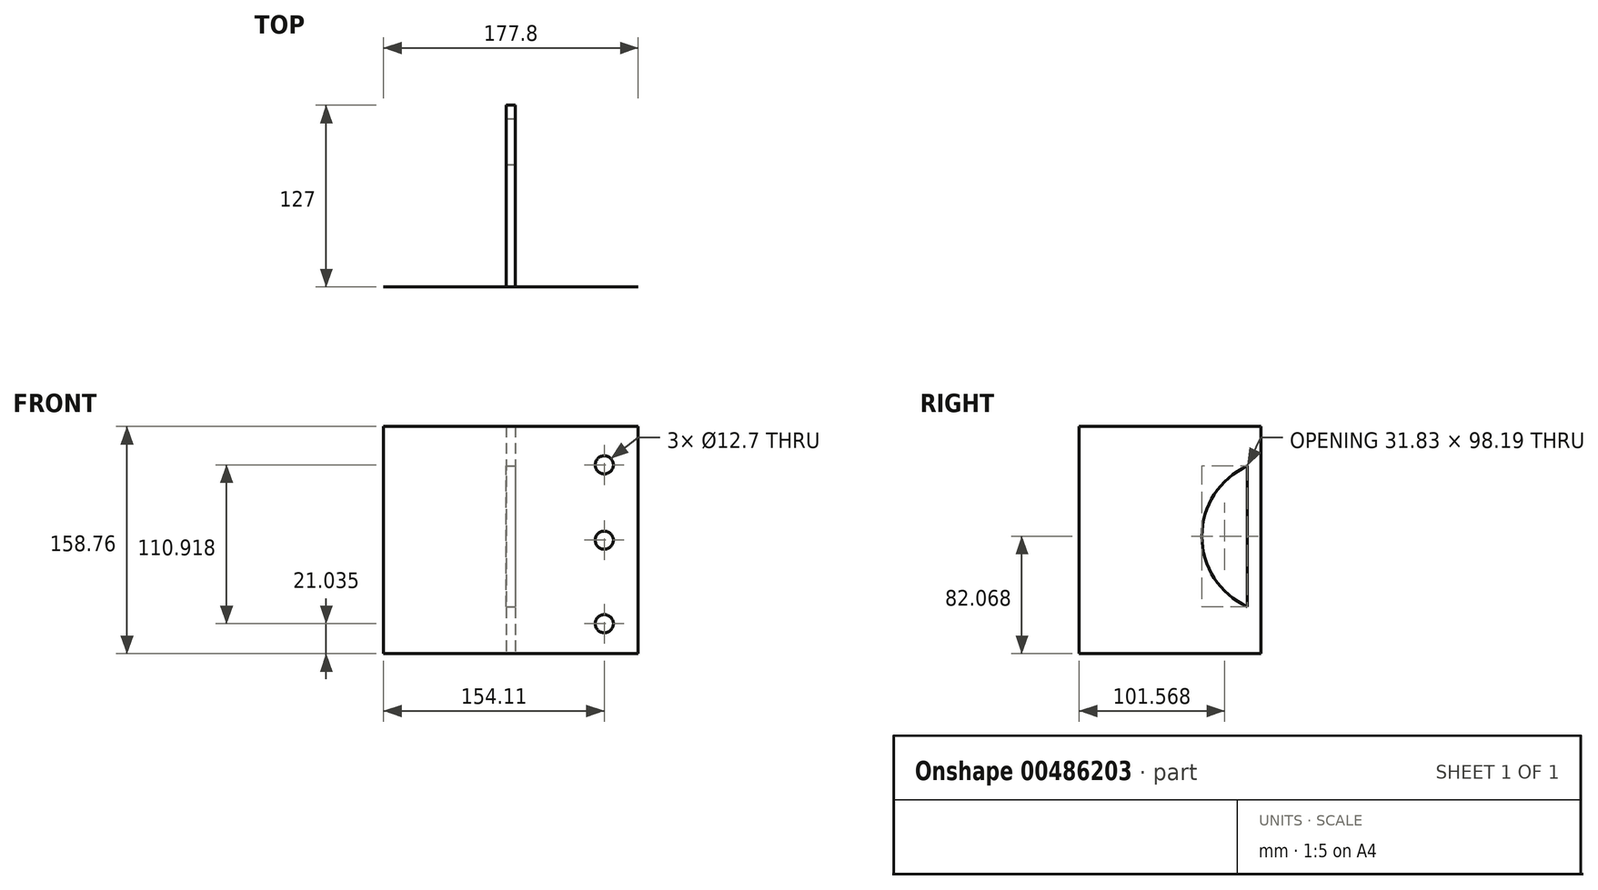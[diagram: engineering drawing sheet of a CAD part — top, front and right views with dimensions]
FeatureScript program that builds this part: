
annotation { "Feature Type Name" : "Feature", "Feature Type Description" : "" }
export const myFeature = defineFeature(function(context is Context, id is Id, definition is map)
    precondition{}
    {
        {
            var Q0;
            Q0=qCreatedBy(makeId("Front.planeOp"),FACE);
            var sketch = newSketch(context, id + "F0", { "sketchPlane" : qUnion([Q0])});
            skLineSegment(sketch, "E0.bottom", {"start": v(-88.9, 79.38) * mm, "end": v(88.9, 79.38) * mm});
            skLineSegment(sketch, "E0.top", {"start": v(-88.9, -79.37) * mm, "end": v(88.9, -79.37) * mm});
            skLineSegment(sketch, "E0.left", {"start": v(-88.9, 79.38) * mm, "end": v(-88.9, -79.37) * mm});
            skLineSegment(sketch, "E0.right", {"start": v(88.9, 79.37) * mm, "end": v(88.9, -79.37) * mm});
            skPoint(sketch, "E0.middle", {"position": v(0, 0) * mm});
            skSolve(sketch);
        }
        {
            var Q0;
            Q0 = qSketchRegion(id + "F0", true);
            extrude(context, id + "F1", {"entities" : qUnion([Q0]), "depth" : 3 / 203.2 * mm, "offsetDistance" : 25.4 * mm});
        }
        {
            var Q0;
            Q0=makeQuery(id+"F1.opExtrude","CAP_FACE",FACE,{"disambiguationData":[OSD([sQuery(id+"F0.wireOp",EDGE,"E0.bottom"),sQuery(id+"F0.wireOp",EDGE,"E0.top"),sQuery(id+"F0.wireOp",EDGE,"E0.left"),sQuery(id+"F0.wireOp",EDGE,"E0.right")])],"isStart":false});
            var sketch = newSketch(context, id + "F2", { "sketchPlane" : qUnion([Q0])});
            skLineSegment(sketch, "E1", {"start": v(0, 79.38) * mm, "end": v(0, -79.37) * mm, "construction": true});
            skLineSegment(sketch, "E2.bottom", {"start": v(3.17, 79.38) * mm, "end": v(-3.18, 79.38) * mm});
            skLineSegment(sketch, "E2.top", {"start": v(3.17, -79.37) * mm, "end": v(-3.18, -79.37) * mm});
            skLineSegment(sketch, "E2.left", {"start": v(3.17, 79.38) * mm, "end": v(3.17, -79.37) * mm});
            skLineSegment(sketch, "E2.right", {"start": v(-3.18, 79.38) * mm, "end": v(-3.18, -79.37) * mm});
            skPoint(sketch, "E2.middle", {"position": v(0, 0) * mm});
            skSolve(sketch);
        }
        {
            var Q0;
            Q0=makeQuery(id+"F2.imprint","IMPRINT",FACE,{"disambiguationData":[TD([[makeQuery(id+"F2.imprint","IMPRINT",EDGE,{"derivedFrom":sQuery(id+"F2.wireOp",EDGE,"E2.bottom")}),-1.0]])]});
            extrude(context, id + "F3", {"entities" : qUnion([Q0]), "operationType" : NewBodyOperationType.ADD, "oppositeDirection" : true, "depth" : 127 * mm, "offsetDistance" : 25.4 * mm});
        }
        {
            var Q0;
            Q0=makeQuery(id+"F3.opExtrude","SWEPT_FACE",FACE,{"disambiguationData":[OSD([sQuery(id+"F2.wireOp",EDGE,"E2.left")])]});
            var sketch = newSketch(context, id + "F4", { "sketchPlane" : qUnion([Q0])});
            skArc(sketch, "E3", {"start": v(117.47, 51.78) * mm, "mid": v(85.64, 2.69) * mm, "end": v(117.47, -46.4) * mm});
            skLineSegment(sketch, "E4", {"start": v(117.47, 51.78) * mm, "end": v(117.47, -46.4) * mm});
            skSolve(sketch);
        }
        {
            var Q0;
            Q0=makeQuery(id+"F4.imprint","IMPRINT",FACE,{"disambiguationData":[TD([[makeQuery(id+"F4.imprint","IMPRINT",EDGE,{"derivedFrom":sQuery(id+"F4.wireOp",EDGE,"E3")}),1.0]])]});
            extrude(context, id + "F5", {"entities" : qUnion([Q0]), "operationType" : NewBodyOperationType.REMOVE, "oppositeDirection" : true, "depth" : 25.4 * mm, "offsetDistance" : 25.4 * mm});
        }
        {
            var Q0;
            {var subQ0=sQuery(id+"F0.wireOp",EDGE,"E0.top");var subQ1=sQuery(id+"F0.wireOp",EDGE,"E0.right");var subQ2=sQuery(id+"F0.wireOp",EDGE,"E0.bottom");Q0=makeQuery(id+"F3.boolean.opBoolean","SPLIT",FACE,{"disambiguationData":[TD([makeQuery(id+"F1.opExtrude","SWEPT_FACE",FACE,{"disambiguationData":[OSD([subQ1])]})])],"derivedFrom":makeQuery(id+"F1.opExtrude","CAP_FACE",FACE,{"disambiguationData":[OSD([subQ2,subQ0,sQuery(id+"F0.wireOp",EDGE,"E0.left"),subQ1])],"isStart":true})});}
            var sketch = newSketch(context, id + "F6", { "sketchPlane" : qUnion([Q0])});
            skCircle(sketch, "E5", {"center": v(-65.2, 52.57) * mm, "radius": 6.35 * mm});
            skLineSegment(sketch, "E6", {"start": v(-65.2, 79.38) * mm, "end": v(-65.2, -79.37) * mm, "construction": true});
            skCircle(sketch, "E7", {"center": v(-65.2, 0) * mm, "radius": 6.35 * mm});
            skCircle(sketch, "E8", {"center": v(-65.2, -58.34) * mm, "radius": 6.35 * mm});
            skLineSegment(sketch, "E9", {"start": v(0, 79.38) * mm, "end": v(0, -79.37) * mm, "construction": true});
            skCircle(sketch, "E10.MirrorC", {"center": v(65.2, 52.57) * mm, "radius": 6.35 * mm});
            skCircle(sketch, "E11.MirrorC", {"center": v(65.2, 0) * mm, "radius": 6.35 * mm});
            skCircle(sketch, "E12.MirrorC", {"center": v(65.2, -58.34) * mm, "radius": 6.35 * mm});
            skSolve(sketch);
        }
        {
            var Q0;
            Q0=makeQuery(id+"F6.imprint","IMPRINT",FACE,{"disambiguationData":[TD([[makeQuery(id+"F6.imprint","IMPRINT",EDGE,{"derivedFrom":sQuery(id+"F6.wireOp",EDGE,"E5")}),1.0]])]});
            var Q1;
            Q1=makeQuery(id+"F6.imprint","IMPRINT",FACE,{"disambiguationData":[TD([[makeQuery(id+"F6.imprint","IMPRINT",EDGE,{"derivedFrom":sQuery(id+"F6.wireOp",EDGE,"E7")}),1.0]])]});
            var Q2;
            Q2=makeQuery(id+"F6.imprint","IMPRINT",FACE,{"disambiguationData":[TD([[makeQuery(id+"F6.imprint","IMPRINT",EDGE,{"derivedFrom":sQuery(id+"F6.wireOp",EDGE,"E8")}),1.0]])]});
            var Q3;
            Q3=makeQuery(id+"F6.imprint","IMPRINT",FACE,{"disambiguationData":[TD([[makeQuery(id+"F6.imprint","IMPRINT",EDGE,{"derivedFrom":sQuery(id+"F6.wireOp",EDGE,"E12.MirrorC")}),-1.0]])]});
            var Q4;
            Q4=makeQuery(id+"F6.imprint","IMPRINT",FACE,{"disambiguationData":[TD([[makeQuery(id+"F6.imprint","IMPRINT",EDGE,{"derivedFrom":sQuery(id+"F6.wireOp",EDGE,"E11.MirrorC")}),-1.0]])]});
            var Q5;
            Q5=makeQuery(id+"F6.imprint","IMPRINT",FACE,{"disambiguationData":[TD([[makeQuery(id+"F6.imprint","IMPRINT",EDGE,{"derivedFrom":sQuery(id+"F6.wireOp",EDGE,"E10.MirrorC")}),-1.0]])]});
            extrude(context, id + "F7", {"entities" : qUnion([Q0, Q1, Q2, Q3, Q4, Q5]), "operationType" : NewBodyOperationType.REMOVE, "oppositeDirection" : true, "depth" : 25.4 * mm, "offsetDistance" : 25.4 * mm});
        }
    });
